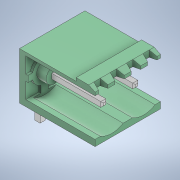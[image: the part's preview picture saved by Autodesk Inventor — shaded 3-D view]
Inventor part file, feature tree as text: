
AUTODESK INVENTOR PART (.ipt)
format: ipt  version: 2020 (Build 240168000, 168)  size: 445,440 bytes
history: native  units: in
note: dims shown in document units (in); Inventor stores cm internally (conversion verified against a paired STEP export)
features: sketch x11, extrude x10, chamfer x2, pattern_linear x1, fillet x1
ambient origin geometry x8: Origin, YZ Plane, XZ Plane, XY Plane, X Axis, Y Axis, Z Axis, Center Point
bodies: Solid1 (feature_tree)
feature tree (25):
  extrude  "Extrusion1"  Depth=0.0394in
  extrude  "Extrusion2"  Depth=0.0394in
  extrude  "Extrusion3"  Depth=0.0197in
  extrude  "Extrusion5"  Depth=0.0197in
  chamfer  "Chamfer2"  Distance=0.4094in
  extrude  "Extrusion6"  Depth=0.2in
  pattern_linear  "Rectangular Pattern1"  Spacing1=0.1181in  [1 undecoded]
  extrude  "Extrusion7"  Depth=0.0039in
  extrude  "Extrusion8"  Depth=0.0039in
  extrude  "Extrusion9"  Depth=0.1575in
  sketch  "Sketch11"  dims[d16=0.0394in d17=0.4094in d18=0.0in]
  chamfer  "Chamfer3"  Distance=0.1575in
  fillet  "Fillet1"  Radius=0.0138in
  extrude  "Extrusion10"  Depth=0.0591in TaperAngle=0.0deg
  extrude  "Extrusion11"  Depth=0.0591in
  sketch  "Sketch1"  dims[d0=0.2953in d1=0.0394in]
  sketch  "Sketch2"  dims[d3=0.3937in d4=0.0394in]
  sketch  "Sketch3"  dims[d5=0.0394in d6=0.0197in]
  sketch  "Sketch5"  dims[d7=0.4331in d10=0.0197in]
  sketch  "Sketch6"  dims[d11=0.4331in]
  sketch  "Sketch7"  dims[d12=0.0197in]
  sketch  "Sketch8"  dims[d14=0.0394in]
  sketch  "Sketch10"  dims[d15=0.1181in]
  sketch  "Sketch12"  dims[d19=0.2in d20=0.1047in]
  sketch  "Sketch13"  dims[d21=0.0in d22=0.1181in d23=0.1in d24=0.1in d25=0.1575in d26=0.1575in d27=0.0472in d28=0.0472in d29=0.0236in d30=0.0236in d31=0.0394in d32=0.0197in d33=0.0138in d34=0.0in d35=0.0591in d36=0.0in d49=0.0591in d50=0.0591in d51=0.0157in d52=0.0315in d53=0.0315in d54=0.0157in d55=0.0315in d56=0.0315in d57=0.0157in d58=0.315in d59=0.0in d60=0.0079in d61=0.0787in d62=45.0deg d69=0.0591in d70=0.0394in d71=0.0098in d72=0.0217in d73=0.1969in d74=0.0in d75=1.5748in d77=0.1024in d78=0.2756in d79=0.2756in d80=0.4193in d81=0.0in d83=0.0394in d84=0.0315in d85=0.0315in d86=0.089in d87=0.089in d88=0.089in d89=0.089in d90=0.1772in d91=0.0in d92=0.0315in d93=0.0315in d96=0.315in d101=0.0157in d102=0.0157in d103=0.0157in d104=0.0315in d105=0.0in d106=0.315in d107=0.0079in d108=0.0787in d109=45.0deg d110=0.0079in d111=0.0591in d112=0.0591in d113=0.0in d114=0.0in d115=0.0197in d116=0.0197in d117=0.0138in d118=0.0138in d128=0.0039in d129=0.0in d130=0.0138in d131=0.0in d132=0.0138in d133=0.0039in d134=0.0in]
note: 1 required parameter value undecoded (feature->parameter linkage not recoverable at this tier; creation-order binding heuristic only, values carry confidence <= 0.55)
